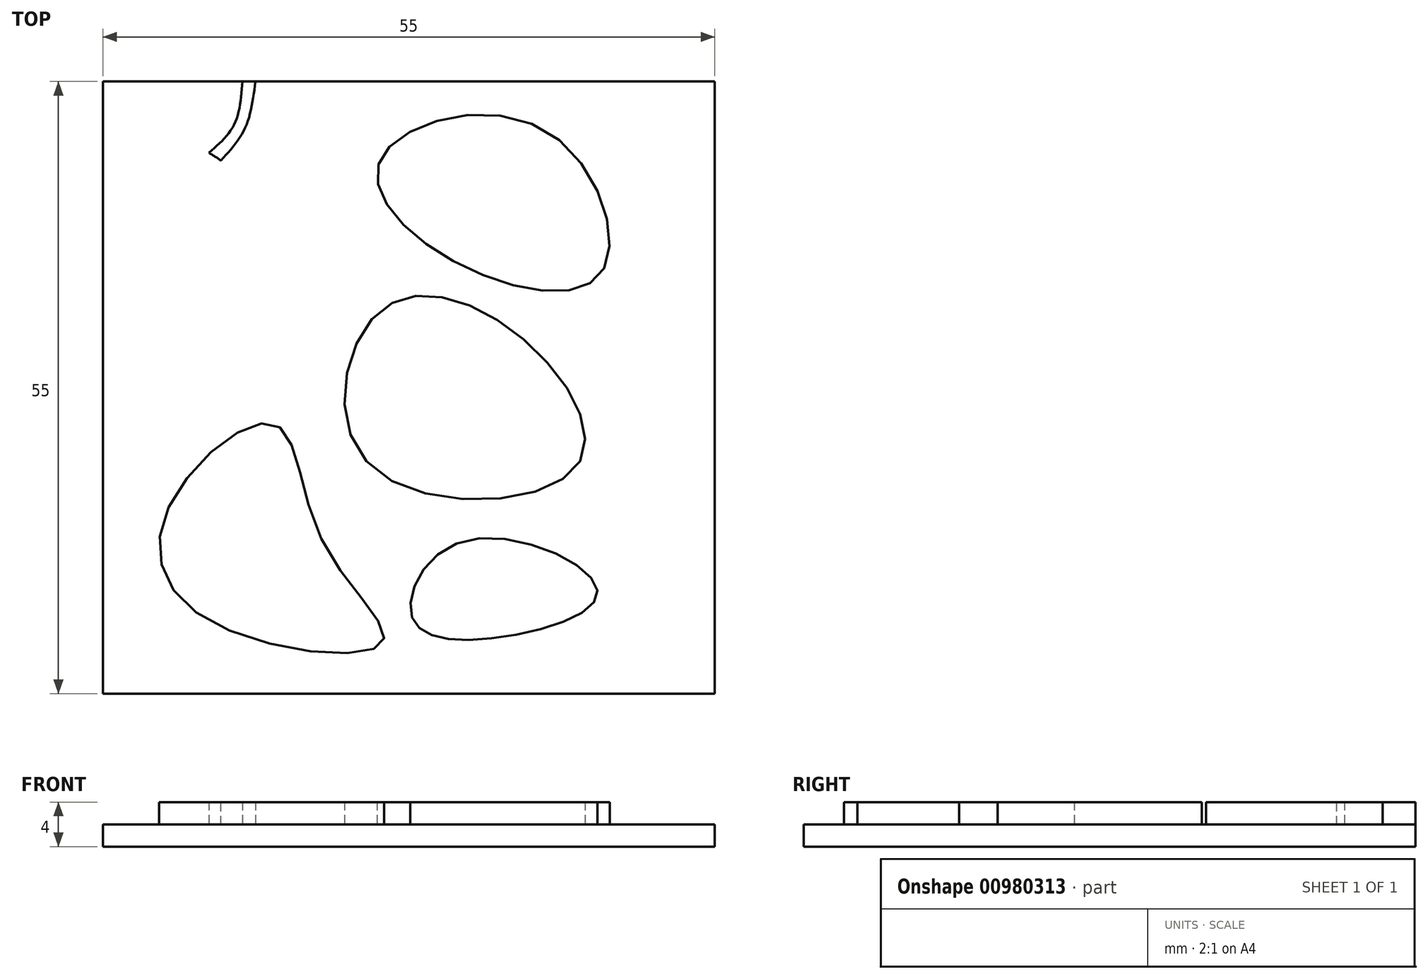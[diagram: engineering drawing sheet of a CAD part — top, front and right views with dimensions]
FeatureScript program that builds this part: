
annotation { "Feature Type Name" : "Feature", "Feature Type Description" : "" }
export const myFeature = defineFeature(function(context is Context, id is Id, definition is map)
    precondition{}
    {
        {
            var Q0;
            Q0=qCreatedBy(makeId("Top.planeOp"),FACE);
            var sketch = newSketch(context, id + "F0", { "sketchPlane" : qUnion([Q0])});
            skLineSegment(sketch, "E0.bottom", {"start": v(-27.78, 41.27) * mm, "end": v(27.22, 41.27) * mm});
            skLineSegment(sketch, "E0.top", {"start": v(-27.78, -13.73) * mm, "end": v(27.22, -13.73) * mm});
            skLineSegment(sketch, "E0.left", {"start": v(-27.78, 41.27) * mm, "end": v(-27.78, -13.73) * mm});
            skLineSegment(sketch, "E0.right", {"start": v(27.22, 41.27) * mm, "end": v(27.22, -13.73) * mm});
            skSolve(sketch);
        }
        {
            var Q0;
            Q0=makeQuery(id+"F0.imprint","IMPRINT",FACE,{"disambiguationData":[TD([[makeQuery(id+"F0.imprint","IMPRINT",EDGE,{"derivedFrom":sQuery(id+"F0.wireOp",EDGE,"E0.bottom")}),-1.0]])]});
            extrude(context, id + "F1", {"entities" : qUnion([Q0]), "depth" : 2 * mm, "offsetDistance" : 25 * mm});
        }
        {
            var Q0;
            Q0=makeQuery(id+"F1.opExtrude","CAP_FACE",FACE,{"disambiguationData":[OSD([sQuery(id+"F0.wireOp",EDGE,"E0.bottom"),sQuery(id+"F0.wireOp",EDGE,"E0.top"),sQuery(id+"F0.wireOp",EDGE,"E0.left"),sQuery(id+"F0.wireOp",EDGE,"E0.right")])],"isStart":false});
            var sketch = newSketch(context, id + "F2", { "sketchPlane" : qUnion([Q0])});
            skFitSpline(sketch, "E1", {"points": [v(-27.78, 29.92) * mm, v(-22.53, 35.46) * mm, v(-10.1, 23.15) * mm, v(-27.78, 17.04) * mm], "startDerivative": vector(14.61, 35.53) * mm, "endDerivative": vector(-68.9, -6.55) * mm});
            skFitSpline(sketch, "E2.0", {"points": [v(-28.7, 30.3) * mm, v(-28.4, 31.04) * mm, v(-27.93, 32.17) * mm, v(-27.2, 33.6) * mm, v(-26.54, 34.57) * mm, v(-25.75, 35.44) * mm, v(-24.77, 36.11) * mm, v(-23.77, 36.43) * mm, v(-22.9, 36.5) * mm, v(-22, 36.44) * mm, v(-20.85, 36.14) * mm, v(-19.43, 35.53) * mm, v(-17.96, 34.7) * mm, v(-16, 33.33) * mm, v(-14.1, 31.67) * mm, v(-12.4, 29.85) * mm, v(-11.26, 28.43) * mm, v(-10.32, 27) * mm, v(-9.6, 25.57) * mm, v(-9.22, 24.39) * mm, v(-9.1, 23.45) * mm, v(-9.11, 22.5) * mm, v(-9.43, 21.4) * mm, v(-10.2, 20.31) * mm, v(-11.26, 19.44) * mm, v(-12.52, 18.75) * mm, v(-13.98, 18.18) * mm, v(-16.16, 17.55) * mm, v(-19.25, 16.97) * mm, v(-23.37, 16.46) * mm, v(-26.25, 16.19) * mm, v(-27.69, 16.05) * mm]});
            skLineSegment(sketch, "E3", {"start": v(-27.78, 29.92) * mm, "end": v(-27.78, 32.44) * mm});
            skLineSegment(sketch, "E4", {"start": v(-27.69, 16.05) * mm, "end": v(-27.78, 16.05) * mm});
            skLineSegment(sketch, "E5", {"start": v(-27.78, 16.05) * mm, "end": v(-27.78, 17.04) * mm});
            skFitSpline(sketch, "E6", {"points": [v(10.03, 18.1) * mm, v(-2.66, 20.8) * mm, v(-3.88, 6.9) * mm, v(14.7, 6.53) * mm, v(10.03, 18.1) * mm]});
            skFitSpline(sketch, "E7.0", {"points": [v(12.35, 17.34) * mm, v(10.14, 19.4) * mm, v(7.7, 21.1) * mm, v(5.16, 22.28) * mm, v(3.23, 22.87) * mm, v(1.3, 23.1) * mm, v(-0.57, 22.94) * mm, v(-2.05, 22.4) * mm, v(-3.14, 21.72) * mm, v(-4.14, 20.87) * mm, v(-5.2, 19.55) * mm, v(-6.17, 17.66) * mm, v(-6.82, 15.57) * mm, v(-7.12, 13.36) * mm, v(-7.02, 11.13) * mm, v(-6.55, 9.32) * mm, v(-5.93, 7.96) * mm, v(-5.32, 7) * mm, v(-4.56, 6.13) * mm, v(-3.67, 5.36) * mm, v(-2.68, 4.7) * mm, v(-1.25, 3.97) * mm, v(0.73, 3.29) * mm, v(3.27, 2.81) * mm, v(5.87, 2.66) * mm, v(8.43, 2.8) * mm, v(10.83, 3.25) * mm, v(12.62, 3.87) * mm, v(13.87, 4.53) * mm, v(14.7, 5.1) * mm, v(15.42, 5.8) * mm, v(15.98, 6.58) * mm, v(16.35, 7.44) * mm, v(16.62, 8.64) * mm, v(16.56, 10.19) * mm, v(16, 12.04) * mm, v(15.07, 13.87) * mm, v(13.83, 15.65) * mm, v(12.35, 17.34) * mm, v(10.14, 19.4) * mm, v(7.7, 21.1) * mm, v(12.35, 17.34) * mm]});
            skFitSpline(sketch, "E8", {"points": [v(3.7, 25.14) * mm, v(-2.84, 34.28) * mm, v(11.62, 37.08) * mm, v(17.04, 24.1) * mm, v(3.7, 25.14) * mm]});
            skFitSpline(sketch, "E9", {"points": [v(-21.87, 3.02) * mm, v(-18.6, -6.96) * mm, v(-2.66, -9.2) * mm, v(-8.06, 0) * mm, v(-12.45, 10.49) * mm, v(-21.87, 3.02) * mm]});
            skFitSpline(sketch, "E10", {"points": [v(7.15, -8.77) * mm, v(16.68, -4.47) * mm, v(4.77, 0) * mm, v(0, -6.82) * mm, v(7.15, -8.77) * mm]});
            skFitSpline(sketch, "E11.0", {"points": [v(6.56, 22.64) * mm, v(3.81, 23.86) * mm, v(1.33, 25.37) * mm, v(-0.36, 26.62) * mm, v(-1.81, 27.98) * mm, v(-2.98, 29.41) * mm, v(-3.82, 30.92) * mm, v(-4.16, 32.26) * mm, v(-4.15, 33.35) * mm, v(-3.98, 34.17) * mm, v(-3.65, 34.95) * mm, v(-3.17, 35.66) * mm, v(-2.57, 36.3) * mm, v(-1.64, 37.08) * mm, v(-0.27, 37.9) * mm, v(1.66, 38.65) * mm, v(3.78, 39.15) * mm, v(6.01, 39.35) * mm, v(8.28, 39.23) * mm, v(10.14, 38.8) * mm, v(11.56, 38.25) * mm, v(12.58, 37.71) * mm, v(13.52, 37.07) * mm, v(14.69, 36.1) * mm, v(15.95, 34.7) * mm, v(17.17, 32.82) * mm, v(18.07, 30.83) * mm, v(18.63, 28.83) * mm, v(18.8, 27.2) * mm, v(18.74, 25.97) * mm, v(18.58, 25.09) * mm, v(18.3, 24.26) * mm, v(17.86, 23.5) * mm, v(17.29, 22.84) * mm, v(16.61, 22.32) * mm, v(15.85, 21.94) * mm, v(14.76, 21.58) * mm, v(13.27, 21.38) * mm, v(11.35, 21.47) * mm, v(9.32, 21.84) * mm, v(6.56, 22.64) * mm, v(3.81, 23.86) * mm, v(1.33, 25.37) * mm, v(6.56, 22.64) * mm]});
            skFitSpline(sketch, "E12.0", {"points": [v(-21.64, 5.51) * mm, v(-22.86, 3.46) * mm, v(-23.6, 1.34) * mm, v(-23.8, -0.77) * mm, v(-23.46, -2.82) * mm, v(-22.55, -4.74) * mm, v(-21.34, -6.16) * mm, v(-20.13, -7.17) * mm, v(-19.09, -7.86) * mm, v(-17.94, -8.48) * mm, v(-16.28, -9.23) * mm, v(-14.03, -9.99) * mm, v(-11.23, -10.65) * mm, v(-8.95, -10.98) * mm, v(-7.25, -11.1) * mm, v(-6.05, -11.12) * mm, v(-4.96, -11.07) * mm, v(-3.97, -10.93) * mm, v(-3.24, -10.73) * mm, v(-2.71, -10.5) * mm, v(-2.34, -10.28) * mm, v(-2, -9.98) * mm, v(-1.7, -9.6) * mm, v(-1.53, -9.14) * mm, v(-1.47, -8.69) * mm, v(-1.51, -8.26) * mm, v(-1.64, -7.73) * mm, v(-1.91, -7.12) * mm, v(-2.36, -6.39) * mm, v(-2.9, -5.64) * mm, v(-3.5, -4.85) * mm, v(-4.37, -3.74) * mm, v(-5.3, -2.55) * mm, v(-6.16, -1.3) * mm, v(-6.66, -0.5) * mm, v(-7.03, 0.16) * mm, v(-7.36, 0.82) * mm, v(-7.73, 1.68) * mm, v(-8.1, 2.73) * mm, v(-8.53, 4.15) * mm, v(-8.98, 5.91) * mm, v(-9.4, 7.55) * mm, v(-9.79, 8.74) * mm, v(-10.13, 9.56) * mm, v(-10.57, 10.3) * mm, v(-11.06, 10.84) * mm, v(-11.55, 11.19) * mm, v(-11.96, 11.39) * mm, v(-12.4, 11.52) * mm, v(-13.01, 11.6) * mm, v(-13.77, 11.54) * mm, v(-14.68, 11.3) * mm, v(-15.6, 10.91) * mm, v(-16.82, 10.23) * mm, v(-18.35, 9.1) * mm, v(-20.1, 7.42) * mm, v(-21.64, 5.51) * mm, v(-22.86, 3.46) * mm, v(-23.6, 1.34) * mm, v(-21.64, 5.51) * mm]});
            skFitSpline(sketch, "E13.0", {"points": [v(5.68, -9.9) * mm, v(7.25, -9.78) * mm, v(8.9, -9.56) * mm, v(10.59, -9.23) * mm, v(12.23, -8.82) * mm, v(13.78, -8.32) * mm, v(15.16, -7.72) * mm, v(16.14, -7.13) * mm, v(16.8, -6.56) * mm, v(17.22, -6.08) * mm, v(17.54, -5.5) * mm, v(17.68, -4.95) * mm, v(17.69, -4.49) * mm, v(17.63, -4.02) * mm, v(17.44, -3.5) * mm, v(17.09, -2.92) * mm, v(16.64, -2.4) * mm, v(16.12, -1.92) * mm, v(15.33, -1.31) * mm, v(14.18, -0.61) * mm, v(12.59, 0.11) * mm, v(10.85, 0.7) * mm, v(9.04, 1.1) * mm, v(7.2, 1.29) * mm, v(5.72, 1.22) * mm, v(4.57, 1) * mm, v(3.48, 0.65) * mm, v(2.26, 0.02) * mm, v(1.05, -0.98) * mm, v(0.1, -2.14) * mm, v(-0.6, -3.39) * mm, v(-1.04, -4.67) * mm, v(-1.17, -5.74) * mm, v(-1.1, -6.56) * mm, v(-0.96, -7.17) * mm, v(-0.71, -7.73) * mm, v(-0.25, -8.4) * mm, v(0.51, -9.04) * mm, v(1.61, -9.52) * mm, v(2.84, -9.8) * mm, v(4.2, -9.92) * mm, v(5.68, -9.9) * mm, v(7.25, -9.78) * mm, v(8.9, -9.56) * mm, v(5.68, -9.9) * mm]});
            skFitSpline(sketch, "E14", {"points": [v(-5.5, 18.94) * mm, v(-9.18, 17.86) * mm, v(-13.63, 18.33) * mm], "startDerivative": vector(-7.49, -2.99) * mm, "endDerivative": vector(-8.8, 1.73) * mm});
            skFitSpline(sketch, "E15", {"points": [v(-20.58, 6.8) * mm, v(-23, 11.7) * mm, v(-27.78, 9.93) * mm], "startDerivative": vector(-3.5, 13) * mm, "endDerivative": vector(-10.97, -6.86) * mm});
            skFitSpline(sketch, "E16", {"points": [v(-22.62, -4.44) * mm, v(-24.48, -7.15) * mm, v(-27.78, -6.77) * mm], "startDerivative": vector(-3.01, -6.97) * mm, "endDerivative": vector(-7.29, 2.3) * mm});
            skFitSpline(sketch, "E17", {"points": [v(-6.94, 0) * mm, v(-3.96, 1.53) * mm, v(-1.54, 4.15) * mm], "startDerivative": vector(6.35, 2.6) * mm, "endDerivative": vector(4.42, 5.61) * mm});
            skFitSpline(sketch, "E18", {"points": [v(-6.9, 10.84) * mm, v(-9.18, 14.03) * mm, v(-14.94, 11.18) * mm], "startDerivative": vector(-4.13, 9.98) * mm, "endDerivative": vector(-11.67, -8.56) * mm});
            skFitSpline(sketch, "E19.0", {"points": [v(-19.61, 7.06) * mm, v(-19.76, 7.6) * mm, v(-19.98, 8.43) * mm, v(-20.31, 9.49) * mm, v(-20.6, 10.24) * mm, v(-20.92, 10.95) * mm, v(-21.32, 11.6) * mm, v(-21.74, 12.08) * mm, v(-22.16, 12.4) * mm, v(-22.51, 12.6) * mm, v(-22.9, 12.73) * mm, v(-23.43, 12.83) * mm, v(-24.07, 12.8) * mm, v(-24.8, 12.63) * mm, v(-25.52, 12.36) * mm, v(-26.22, 12.02) * mm, v(-27.16, 11.5) * mm, v(-27.85, 11.06) * mm, v(-28.31, 10.78) * mm]});
            skFitSpline(sketch, "E20.0", {"points": [v(-21.7, -4.83) * mm, v(-21.83, -5.12) * mm, v(-22.1, -5.72) * mm, v(-22.47, -6.47) * mm, v(-22.84, -7.03) * mm, v(-23.18, -7.43) * mm, v(-23.51, -7.73) * mm, v(-23.82, -7.93) * mm, v(-24.08, -8.07) * mm, v(-24.34, -8.17) * mm, v(-24.7, -8.27) * mm, v(-25.15, -8.32) * mm, v(-25.67, -8.3) * mm, v(-26.34, -8.22) * mm, v(-27.15, -8.02) * mm, v(-27.78, -7.82) * mm, v(-28.08, -7.73) * mm]});
            skFitSpline(sketch, "E21.0", {"points": [v(-6.56, -0.93) * mm, v(-6.3, -0.82) * mm, v(-5.75, -0.6) * mm, v(-4.93, -0.23) * mm, v(-4.24, 0.14) * mm, v(-3.7, 0.48) * mm, v(-3.3, 0.77) * mm, v(-2.92, 1.08) * mm, v(-2.45, 1.52) * mm, v(-1.9, 2.1) * mm, v(-1.31, 2.82) * mm, v(-0.94, 3.3) * mm, v(-0.75, 3.53) * mm]});
            skFitSpline(sketch, "E22.0", {"points": [v(-5.97, 11.22) * mm, v(-6.14, 11.64) * mm, v(-6.4, 12.28) * mm, v(-6.82, 13.11) * mm, v(-7.18, 13.7) * mm, v(-7.62, 14.25) * mm, v(-8.1, 14.64) * mm, v(-8.54, 14.88) * mm, v(-8.92, 15) * mm, v(-9.32, 15.08) * mm, v(-9.83, 15.09) * mm, v(-10.45, 15) * mm, v(-11.17, 14.75) * mm, v(-11.89, 14.42) * mm, v(-12.84, 13.88) * mm, v(-14.06, 13.06) * mm, v(-15.04, 12.34) * mm, v(-15.53, 11.98) * mm]});
            skFitSpline(sketch, "E23.0", {"points": [v(-5.86, 19.87) * mm, v(-6.17, 19.75) * mm, v(-6.79, 19.5) * mm, v(-7.67, 19.18) * mm, v(-8.4, 18.99) * mm, v(-8.97, 18.88) * mm, v(-9.54, 18.82) * mm, v(-10.3, 18.82) * mm, v(-11.3, 18.92) * mm, v(-12.34, 19.1) * mm, v(-13.07, 19.24) * mm, v(-13.43, 19.31) * mm]});
            skFitSpline(sketch, "E24", {"points": [v(-5.86, 19.87) * mm, v(-4.63, 20.23) * mm], "startDerivative": vector(1.24, 0.35) * mm, "endDerivative": vector(1.24, 0.35) * mm});
            skFitSpline(sketch, "E25", {"points": [v(-15.53, 11.98) * mm, v(-16.42, 11.26) * mm, v(-16.81, 10.19) * mm], "startDerivative": vector(-2.03, -1.28) * mm, "endDerivative": vector(-0.53, -2.33) * mm});
            skLineSegment(sketch, "E26", {"start": v(-27.78, 9.93) * mm, "end": v(-27.78, 11.1) * mm});
            skLineSegment(sketch, "E27", {"start": v(-27.78, -6.77) * mm, "end": v(-27.78, -7.82) * mm});
            skFitSpline(sketch, "E28", {"points": [v(-0.78, 3.5) * mm, v(-0.63, 3.6) * mm, v(-0.62, 3.77) * mm], "startDerivative": vector(0.32, 0.2) * mm, "endDerivative": vector(-0.05, 0.3) * mm});
            skFitSpline(sketch, "E29", {"points": [v(11.5, 3.51) * mm, v(12.48, 1.63) * mm, v(11.95, 0.32) * mm], "startDerivative": vector(2.6, -3.51) * mm, "endDerivative": vector(-1.95, -3.05) * mm});
            skFitSpline(sketch, "E30", {"points": [v(11.19, 0.57) * mm, v(11.62, 1.67) * mm, v(10.68, 3.28) * mm], "startDerivative": vector(1.87, 2.64) * mm, "endDerivative": vector(-2.27, 3.2) * mm});
            skFitSpline(sketch, "E31", {"points": [v(-1.55, 22.56) * mm, v(-3.52, 25.03) * mm, v(-1.31, 27.53) * mm], "startDerivative": vector(-6.08, 5.12) * mm, "endDerivative": vector(6.5, 4.93) * mm});
            skFitSpline(sketch, "E32", {"points": [v(-0.57, 26.85) * mm, v(-2.23, 25.16) * mm, v(-0.38, 22.9) * mm], "startDerivative": vector(-5.2, -3.4) * mm, "endDerivative": vector(5.4, -4.6) * mm});
            skFitSpline(sketch, "E33", {"points": [v(-3.5, 30.41) * mm, v(-9.82, 35.49) * mm, v(-13.88, 31.39) * mm], "startDerivative": vector(-12.4, 14.33) * mm, "endDerivative": vector(-8.26, -13.17) * mm});
            skFitSpline(sketch, "E34", {"points": [v(-13.09, 30.58) * mm, v(-9.39, 34.1) * mm, v(-4.34, 29.42) * mm, v(-2.4, 28.7) * mm], "startDerivative": vector(9.61, 15.92) * mm, "endDerivative": vector(7.8, -0.42) * mm});
            skFitSpline(sketch, "E35", {"points": [v(-17.19, 34.14) * mm, v(-15, 37.1) * mm, v(-14.07, 41.27) * mm], "startDerivative": vector(5.22, 5.7) * mm, "endDerivative": vector(1.07, 8.52) * mm});
            skFitSpline(sketch, "E36", {"points": [v(-18.27, 34.85) * mm, v(-15.99, 37.4) * mm, v(-15.23, 41.27) * mm], "startDerivative": vector(5.53, 4.77) * mm, "endDerivative": vector(0.62, 8.04) * mm});
            skLineSegment(sketch, "E37", {"start": v(-14.07, 41.27) * mm, "end": v(-15.23, 41.27) * mm});
            skFitSpline(sketch, "E38", {"points": [v(15.53, 35.13) * mm, v(20.96, 37.72) * mm, v(22.68, 41.27) * mm], "startDerivative": vector(11.47, 3.8) * mm, "endDerivative": vector(2.52, 8.66) * mm});
            skFitSpline(sketch, "E39", {"points": [v(14.71, 36.02) * mm, v(19.62, 38.58) * mm, v(20.96, 41.27) * mm], "startDerivative": vector(10.08, 3.92) * mm, "endDerivative": vector(2, 6.74) * mm});
            skFitSpline(sketch, "E40", {"points": [v(1.15, 38.43) * mm, v(-0.7, 39.84) * mm, v(-1.25, 41.27) * mm], "startDerivative": vector(-3.95, 2.37) * mm, "endDerivative": vector(-0.75, 3.34) * mm});
            skFitSpline(sketch, "E41", {"points": [v(0, 37.97) * mm, v(-2.11, 39.13) * mm, v(-2.5, 41.27) * mm], "startDerivative": vector(-4.97, 1.72) * mm, "endDerivative": vector(0, 4.9) * mm});
            skFitSpline(sketch, "E42", {"points": [v(18.74, 26.19) * mm, v(22.68, 23.05) * mm, v(27.22, 23.83) * mm], "startDerivative": vector(7.27, -8.13) * mm, "endDerivative": vector(9.67, 3.5) * mm});
            skFitSpline(sketch, "E43", {"points": [v(18.7, 28.11) * mm, v(22.76, 24.93) * mm, v(27.22, 25.87) * mm], "startDerivative": vector(7.56, -8.27) * mm, "endDerivative": vector(9.53, 3.91) * mm});
            skLineSegment(sketch, "E44", {"start": v(27.22, 23.83) * mm, "end": v(27.22, 25.87) * mm});
            skLineSegment(sketch, "E45", {"start": v(22.68, 41.27) * mm, "end": v(20.96, 41.27) * mm});
            skLineSegment(sketch, "E46", {"start": v(-1.25, 41.27) * mm, "end": v(-2.5, 41.27) * mm});
            skFitSpline(sketch, "E47", {"points": [v(16.03, 6.76) * mm, v(19.7, 3.12) * mm, v(24.96, 2.1) * mm, v(27.22, 3.98) * mm], "startDerivative": vector(8.53, -11.27) * mm, "endDerivative": vector(6.68, 8.7) * mm});
            skFitSpline(sketch, "E48", {"points": [v(16.52, 8.3) * mm, v(20.01, 5.31) * mm, v(24.56, 4.06) * mm, v(27.22, 6.18) * mm], "startDerivative": vector(8.94, -9.16) * mm, "endDerivative": vector(7.7, 9.38) * mm});
            skFitSpline(sketch, "E49", {"points": [v(14.15, 15.16) * mm, v(20.8, 15.1) * mm, v(27.22, 11.85) * mm], "startDerivative": vector(13.19, -1.82) * mm, "endDerivative": vector(13, -5.73) * mm});
            skFitSpline(sketch, "E50", {"points": [v(12.96, 16.63) * mm, v(21, 16.76) * mm, v(27.22, 13.77) * mm], "startDerivative": vector(16.33, 1.59) * mm, "endDerivative": vector(12.18, -7.4) * mm});
            skLineSegment(sketch, "E51", {"start": v(27.22, 3.98) * mm, "end": v(27.22, 6.18) * mm});
            skLineSegment(sketch, "E52", {"start": v(27.22, 11.85) * mm, "end": v(27.22, 13.77) * mm});
            skFitSpline(sketch, "E53", {"points": [v(-11.15, -10.62) * mm, v(-14.01, -11.7) * mm, v(-14.18, -13.73) * mm], "startDerivative": vector(-6.52, -1.3) * mm, "endDerivative": vector(0.71, -5.08) * mm});
            skFitSpline(sketch, "E54", {"points": [v(-9.95, -10.82) * mm, v(-12.68, -12.04) * mm, v(-12.84, -13.73) * mm], "startDerivative": vector(-6.05, -1.62) * mm, "endDerivative": vector(0.56, -4.33) * mm});
            skFitSpline(sketch, "E55", {"points": [v(2, -9.6) * mm, v(1.75, -11.81) * mm, v(2.47, -13.73) * mm], "startDerivative": vector(-1, -4.46) * mm, "endDerivative": vector(1.96, -3.82) * mm});
            skFitSpline(sketch, "E56", {"points": [v(3.3, -9.83) * mm, v(2.91, -11.76) * mm, v(4.13, -13.73) * mm], "startDerivative": vector(-1.58, -4.08) * mm, "endDerivative": vector(3.17, -3.73) * mm});
            skFitSpline(sketch, "E57", {"points": [v(-3.98, -10.91) * mm, v(-1.03, -11.98) * mm, v(0.7, -13.73) * mm], "startDerivative": vector(6.06, -1.56) * mm, "endDerivative": vector(3.22, -4.13) * mm});
            skFitSpline(sketch, "E58", {"points": [v(-5.63, -11.1) * mm, v(-2.03, -12.6) * mm, v(-0.75, -13.73) * mm], "startDerivative": vector(7.82, -1.95) * mm, "endDerivative": vector(1.35, -3.47) * mm});
            skFitSpline(sketch, "E59", {"points": [v(11.6, -8.97) * mm, v(15.62, -9.82) * mm, v(16.61, -13.73) * mm], "startDerivative": vector(9.5, -0.14) * mm, "endDerivative": vector(0.51, -9.4) * mm});
            skFitSpline(sketch, "E60", {"points": [v(9.85, -9.37) * mm, v(12.29, -10.04) * mm, v(14.62, -11.1) * mm, v(15.34, -13.73) * mm], "startDerivative": vector(3.9, -3.75) * mm, "endDerivative": vector(0.12, -9.1) * mm});
            skFitSpline(sketch, "E61", {"points": [v(17.54, -3.8) * mm, v(22.5, -8.1) * mm, v(27.22, -8.99) * mm], "startDerivative": vector(8.9, -9.6) * mm, "endDerivative": vector(10.48, -0.53) * mm});
            skLineSegment(sketch, "E62", {"start": v(16.61, -13.73) * mm, "end": v(15.34, -13.73) * mm});
            skLineSegment(sketch, "E63", {"start": v(4.13, -13.73) * mm, "end": v(2.47, -13.73) * mm});
            skLineSegment(sketch, "E64", {"start": v(0.7, -13.73) * mm, "end": v(-0.75, -13.73) * mm});
            skLineSegment(sketch, "E65", {"start": v(-12.84, -13.73) * mm, "end": v(-14.18, -13.73) * mm});
            skFitSpline(sketch, "E66.0", {"points": [v(16.8, -4.49) * mm, v(17.18, -4.89) * mm, v(17.93, -5.7) * mm, v(19.1, -6.86) * mm, v(20.1, -7.75) * mm, v(20.96, -8.37) * mm, v(21.63, -8.79) * mm, v(22.33, -9.13) * mm, v(23.27, -9.5) * mm, v(24.45, -9.77) * mm, v(25.84, -9.92) * mm, v(26.73, -9.96) * mm, v(27.17, -9.98) * mm]});
            skLineSegment(sketch, "E67", {"start": v(27.17, -9.98) * mm, "end": v(27.22, -9.98) * mm});
            skLineSegment(sketch, "E68", {"start": v(27.22, -9.98) * mm, "end": v(27.22, -8.99) * mm});
            skSolve(sketch);
        }
        {
            var Q0;
            Q0 = qSketchRegion(id + "F2", true);
            extrude(context, id + "F3", {"entities" : qUnion([Q0]), "operationType" : NewBodyOperationType.ADD, "depth" : 2 * mm, "offsetDistance" : 25 * mm});
        }
    });
